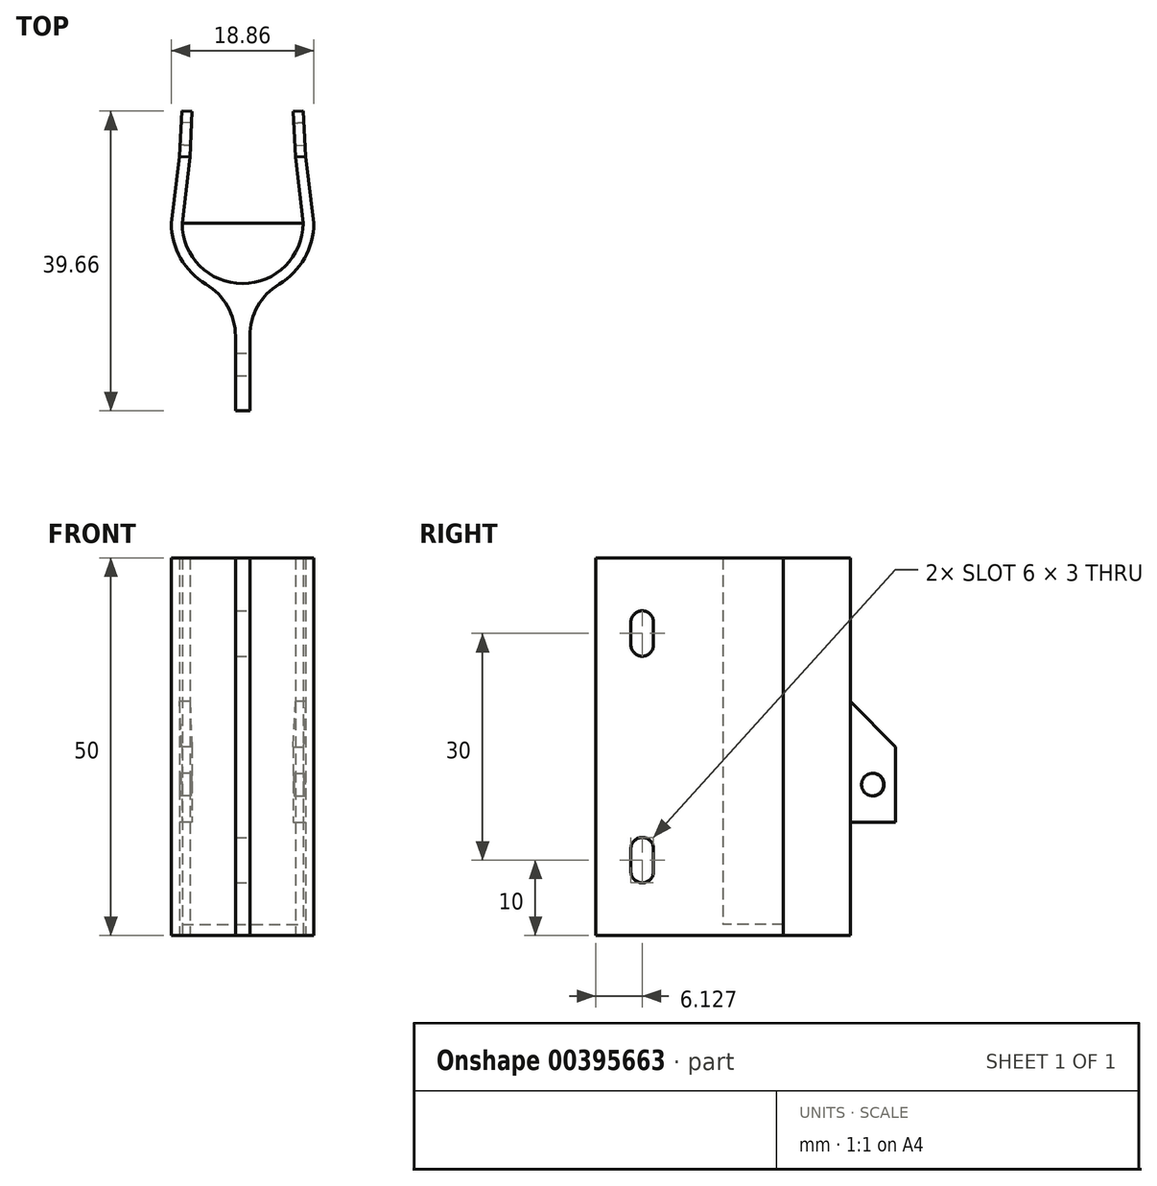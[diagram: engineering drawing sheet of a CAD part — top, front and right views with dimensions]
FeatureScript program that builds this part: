
annotation { "Feature Type Name" : "Feature", "Feature Type Description" : "" }
export const myFeature = defineFeature(function(context is Context, id is Id, definition is map)
    precondition{}
    {
        {
            var Q0;
            Q0=qCreatedBy(makeId("Top.planeOp"),FACE);
            var sketch = newSketch(context, id + "F0", { "sketchPlane" : qUnion([Q0])});
            skArc(sketch, "E0", {"start": v(-13.16, -8.09) * mm, "mid": v(-5.16, -16.09) * mm, "end": v(2.84, -8.09) * mm});
            skLineSegment(sketch, "E1", {"start": v(-13.16, -8.09) * mm, "end": v(-8.87, -8.09) * mm});
            skLineSegment(sketch, "E2", {"start": v(2.84, -8.09) * mm, "end": v(-1.44, -8.09) * mm});
            skLineSegment(sketch, "E3", {"start": v(-13.16, -8.09) * mm, "end": v(-12.15, 0.68) * mm});
            skLineSegment(sketch, "E4", {"start": v(-14.59, -8.09) * mm, "end": v(-13.51, 0.75) * mm});
            skLineSegment(sketch, "E5", {"start": v(-13.51, 0.75) * mm, "end": v(-12.15, 0.68) * mm});
            skLineSegment(sketch, "E6.MirrorCS", {"start": v(2.84, -8.09) * mm, "end": v(1.83, 0.68) * mm});
            skLineSegment(sketch, "E7.MirrorCS", {"start": v(4.27, -8.09) * mm, "end": v(3.2, 0.75) * mm});
            skLineSegment(sketch, "E8.MirrorCS", {"start": v(3.2, 0.75) * mm, "end": v(1.83, 0.68) * mm});
            skLineSegment(sketch, "E9", {"start": v(-4.2, -32.92) * mm, "end": v(-4.2, -17.47) * mm});
            skLineSegment(sketch, "E10", {"start": v(-6.1, -32.92) * mm, "end": v(-6.1, -17.47) * mm});
            skLineSegment(sketch, "E11", {"start": v(-6.1, -32.92) * mm, "end": v(-4.2, -32.92) * mm});
            skArc(sketch, "E12", {"start": v(-14.59, -8.09) * mm, "mid": v(-12.15, -14.41) * mm, "end": v(-6.1, -17.47) * mm});
            skArc(sketch, "E13", {"start": v(4.27, -8.09) * mm, "mid": v(1.84, -14.41) * mm, "end": v(-4.2, -17.47) * mm});
            skLineSegment(sketch, "E14", {"start": v(-8.87, -8.09) * mm, "end": v(-1.44, -8.09) * mm});
            skSolve(sketch);
        }
        {
            var Q0;
            Q0=makeQuery(id+"F0.imprint","IMPRINT",FACE,{"disambiguationData":[TD([[makeQuery(id+"F0.imprint","IMPRINT",EDGE,{"derivedFrom":sQuery(id+"F0.wireOp",EDGE,"E0")}),1.0]])]});
            extrude(context, id + "F1", {"entities" : qUnion([Q0]), "depth" : 1.5 * mm});
        }
        {
            var Q0;
            Q0=makeQuery(id+"F0.imprint","IMPRINT",FACE,{"disambiguationData":[TD([[makeQuery(id+"F0.imprint","IMPRINT",EDGE,{"derivedFrom":sQuery(id+"F0.wireOp",EDGE,"E0")}),-1.0]])]});
            extrude(context, id + "F2", {"entities" : qUnion([Q0]), "operationType" : NewBodyOperationType.ADD, "depth" : 50 * mm});
        }
        {
            var Q0;
            Q0=makeQuery(id+"F2.opExtrude","SWEPT_EDGE",EDGE,{"disambiguationData":[OSD([sQuery(id+"F0.wireOp",EDGE,"E10"),sQuery(id+"F0.wireOp",EDGE,"E12")])]});
            var Q1;
            Q1=makeQuery(id+"F2.opExtrude","SWEPT_EDGE",EDGE,{"disambiguationData":[OSD([sQuery(id+"F0.wireOp",EDGE,"E9"),sQuery(id+"F0.wireOp",EDGE,"E13")])]});
            fillet(context, id + "F3", {"entities" : qUnion([Q0, Q1]), "radius" : 8 * mm, "tangentPropagation" : true, "allowEdgeOverflow" : false});
        }
        {
            var Q0;
            Q0=makeQuery(id+"F2.opExtrude","SWEPT_FACE",FACE,{"disambiguationData":[OSD([sQuery(id+"F0.wireOp",EDGE,"E8.MirrorCS")])]});
            var sketch = newSketch(context, id + "F4", { "sketchPlane" : qUnion([Q0])});
            skLineSegment(sketch, "E15.bottom", {"start": v(-1.86, 15) * mm, "end": v(-3.23, 15) * mm});
            skLineSegment(sketch, "E15.top", {"start": v(-1.86, 25) * mm, "end": v(-3.23, 25) * mm});
            skLineSegment(sketch, "E15.left", {"start": v(-1.86, 15) * mm, "end": v(-1.86, 25) * mm});
            skLineSegment(sketch, "E15.right", {"start": v(-3.23, 15) * mm, "end": v(-3.23, 25) * mm});
            skSolve(sketch);
        }
        {
            var Q0;
            Q0=makeQuery(id+"F2.opExtrude","SWEPT_FACE",FACE,{"disambiguationData":[OSD([sQuery(id+"F0.wireOp",EDGE,"E5")])]});
            var sketch = newSketch(context, id + "F5", { "sketchPlane" : qUnion([Q0])});
            skLineSegment(sketch, "E16.bottom", {"start": v(12.16, 15) * mm, "end": v(13.53, 15) * mm});
            skLineSegment(sketch, "E16.top", {"start": v(12.16, 25) * mm, "end": v(13.53, 25) * mm});
            skLineSegment(sketch, "E16.left", {"start": v(12.16, 15) * mm, "end": v(12.16, 25) * mm});
            skLineSegment(sketch, "E16.right", {"start": v(13.53, 15) * mm, "end": v(13.53, 25) * mm});
            skSolve(sketch);
        }
        {
            var Q0;
            Q0=makeQuery(id+"F4.imprint","IMPRINT",FACE,{"disambiguationData":[TD([[makeQuery(id+"F4.imprint","IMPRINT",EDGE,{"derivedFrom":sQuery(id+"F4.wireOp",EDGE,"E15.bottom")}),-1.0]])]});
            extrude(context, id + "F6", {"entities" : qUnion([Q0]), "operationType" : NewBodyOperationType.ADD, "depth" : 6 * mm});
        }
        {
            var Q0;
            Q0 = qSketchRegion(id + "F5", true);
            extrude(context, id + "F7", {"entities" : qUnion([Q0]), "operationType" : NewBodyOperationType.ADD, "depth" : 6 * mm});
        }
        {
            var Q0;
            Q0=makeQuery(id+"F6.opExtrude","SWEPT_FACE",FACE,{"disambiguationData":[OSD([sQuery(id+"F4.wireOp",EDGE,"E15.right")])]});
            var sketch = newSketch(context, id + "F8", { "sketchPlane" : qUnion([Q0])});
            skCircle(sketch, "E17", {"center": v(3.59, 20) * mm, "radius": 1.5 * mm});
            skSolve(sketch);
        }
        {
            var Q0;
            Q0=makeQuery(id+"F8.imprint","IMPRINT",FACE,{"disambiguationData":[TD([[makeQuery(id+"F8.imprint","IMPRINT",EDGE,{"derivedFrom":sQuery(id+"F8.wireOp",EDGE,"E17")}),1.0]])]});
            extrude(context, id + "F9", {"entities" : qUnion([Q0]), "operationType" : NewBodyOperationType.REMOVE, "oppositeDirection" : true, "depth" : 2 * mm});
        }
        {
            var Q0;
            Q0=makeQuery(id+"F7.opExtrude","SWEPT_FACE",FACE,{"disambiguationData":[OSD([sQuery(id+"F5.wireOp",EDGE,"E16.right")])]});
            var sketch = newSketch(context, id + "F10", { "sketchPlane" : qUnion([Q0])});
            skCircle(sketch, "E18", {"center": v(-3.07, 20) * mm, "radius": 1.5 * mm});
            skSolve(sketch);
        }
        {
            var Q0;
            Q0=makeQuery(id+"F10.imprint","IMPRINT",FACE,{"disambiguationData":[TD([[makeQuery(id+"F10.imprint","IMPRINT",EDGE,{"derivedFrom":sQuery(id+"F10.wireOp",EDGE,"E18")}),1.0]])]});
            extrude(context, id + "F11", {"entities" : qUnion([Q0]), "operationType" : NewBodyOperationType.REMOVE, "oppositeDirection" : true, "depth" : 2 * mm});
        }
        {
            var Q0;
            Q0=makeQuery(id+"F6.opExtrude","CAP_EDGE",EDGE,{"disambiguationData":[OSD([sQuery(id+"F4.wireOp",EDGE,"E15.bottom")])],"isStart":true});
            var Q1;
            Q1=makeQuery(id+"F7.opExtrude","CAP_EDGE",EDGE,{"disambiguationData":[OSD([sQuery(id+"F5.wireOp",EDGE,"E16.bottom")])],"isStart":true});
            var Q2;
            Q2=makeQuery(id+"F6.opExtrude","CAP_EDGE",EDGE,{"disambiguationData":[OSD([sQuery(id+"F4.wireOp",EDGE,"E15.top")])],"isStart":true});
            var Q3;
            Q3=makeQuery(id+"F7.opExtrude","CAP_EDGE",EDGE,{"disambiguationData":[OSD([sQuery(id+"F5.wireOp",EDGE,"E16.top")])],"isStart":true});
            chamfer(context, id + "F12", {"entities" : qUnion([Q0, Q1, Q2, Q3]), "width" : 6 * mm, "tangentPropagation" : true});
        }
        {
            var Q0;
            Q0=makeQuery(id+"F2.opExtrude","SWEPT_FACE",FACE,{"disambiguationData":[OSD([sQuery(id+"F0.wireOp",EDGE,"E9")])]});
            var sketch = newSketch(context, id + "F13", { "sketchPlane" : qUnion([Q0])});
            skLineSegment(sketch, "E19.left", {"start": v(-25.3, 38.5) * mm, "end": v(-25.3, 41.5) * mm});
            skLineSegment(sketch, "E19.right", {"start": v(-28.3, 38.5) * mm, "end": v(-28.3, 41.5) * mm});
            skPoint(sketch, "E19.middle", {"position": v(-26.8, 40) * mm});
            skLineSegment(sketch, "E20.left", {"start": v(-25.3, 8.5) * mm, "end": v(-25.3, 11.5) * mm});
            skLineSegment(sketch, "E20.right", {"start": v(-28.3, 8.5) * mm, "end": v(-28.3, 11.5) * mm});
            skPoint(sketch, "E20.middle", {"position": v(-26.8, 10) * mm});
            skArc(sketch, "E21", {"start": v(-28.3, 41.5) * mm, "mid": v(-26.8, 43) * mm, "end": v(-25.3, 41.5) * mm});
            skArc(sketch, "E22", {"start": v(-25.3, 38.5) * mm, "mid": v(-26.8, 37) * mm, "end": v(-28.3, 38.5) * mm});
            skArc(sketch, "E23", {"start": v(-25.3, 11.5) * mm, "mid": v(-26.8, 13) * mm, "end": v(-28.3, 11.5) * mm});
            skArc(sketch, "E24", {"start": v(-25.3, 8.5) * mm, "mid": v(-26.8, 7) * mm, "end": v(-28.3, 8.5) * mm});
            skSolve(sketch);
        }
        {
            var Q0;
            Q0=makeQuery(id+"F13.imprint","IMPRINT",FACE,{"disambiguationData":[TD([[makeQuery(id+"F13.imprint","IMPRINT",EDGE,{"derivedFrom":sQuery(id+"F13.wireOp",EDGE,"E19.left")}),1.0]])]});
            var Q1;
            Q1=makeQuery(id+"F13.imprint","IMPRINT",FACE,{"disambiguationData":[TD([[makeQuery(id+"F13.imprint","IMPRINT",EDGE,{"derivedFrom":sQuery(id+"F13.wireOp",EDGE,"E20.left")}),1.0]])]});
            extrude(context, id + "F14", {"entities" : qUnion([Q0, Q1]), "operationType" : NewBodyOperationType.REMOVE, "oppositeDirection" : true, "depth" : 3 * mm});
        }
    });
